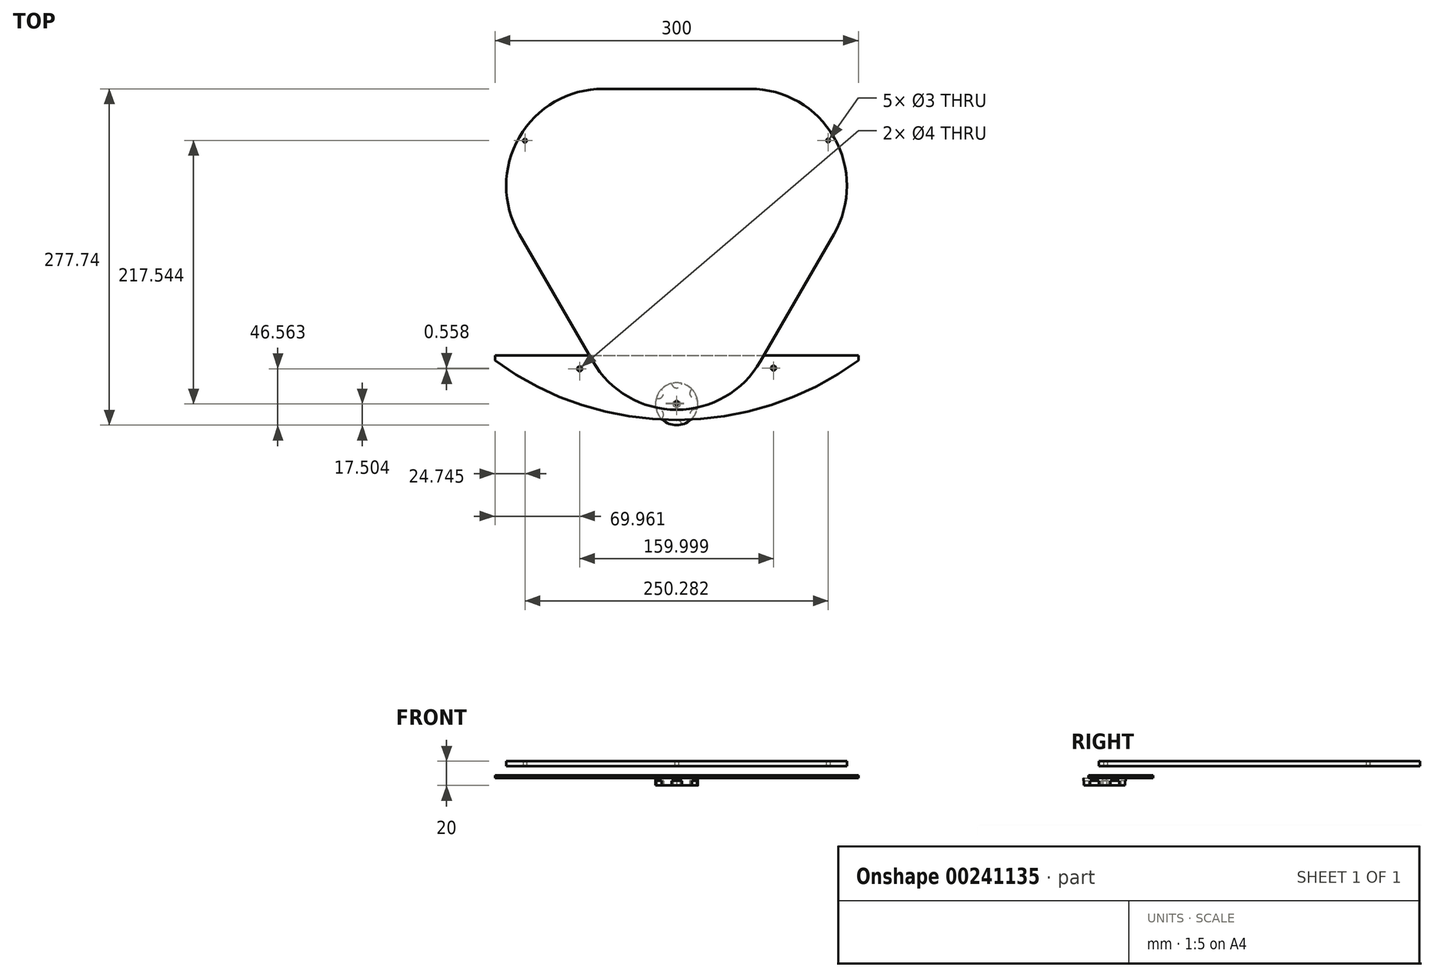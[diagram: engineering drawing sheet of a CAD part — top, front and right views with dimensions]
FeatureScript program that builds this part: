
annotation { "Feature Type Name" : "Feature", "Feature Type Description" : "" }
export const myFeature = defineFeature(function(context is Context, id is Id, definition is map)
    precondition{}
    {
        {
            var Q0;
            Q0=qCreatedBy(makeId("Top.planeOp"),FACE);
            var sketch = newSketch(context, id + "F0", { "sketchPlane" : qUnion([Q0])});
            skLineSegment(sketch, "E0.bottom", {"start": v(-210.81, -28.63) * mm, "end": v(89.19, -28.63) * mm});
            skCircle(sketch, "E1", {"center": v(-140.85, -39.57) * mm, "radius": 2 * mm});
            skCircle(sketch, "E2.MirrorC", {"center": v(19.15, -39) * mm, "radius": 2 * mm});
            skArc(sketch, "E3.2.3", {"start": v(-210.81, -32.82) * mm, "mid": v(-60.8, -81.83) * mm, "end": v(89.19, -32.72) * mm});
            skLineSegment(sketch, "E4", {"start": v(-210.81, -32.82) * mm, "end": v(-210.81, -28.63) * mm});
            skLineSegment(sketch, "E5", {"start": v(89.19, -32.72) * mm, "end": v(89.19, -28.63) * mm});
            skLineSegment(sketch, "E6.0", {"start": v(-210.81, -48.63) * mm, "end": v(89.19, -48.63) * mm, "construction": true});
            skCircle(sketch, "E7", {"center": v(-60.81, -68.63) * mm, "radius": 17.5 * mm});
            skPoint(sketch, "E7.centerSnap0", {"position": v(-60.81, -48.63) * mm});
            skCircle(sketch, "E8", {"center": v(-60.81, -68.63) * mm, "radius": 1.5 * mm});
            skSolve(sketch);
        }
        {
            var Q0;
            Q0=makeQuery(id+"F0.imprint","IMPRINT",FACE,{"disambiguationData":[TD([[makeQuery(id+"F0.imprint","IMPRINT",EDGE,{"derivedFrom":sQuery(id+"F0.wireOp",EDGE,"E0.bottom")}),-1.0]])]});
            var Q1;
            Q1=makeQuery(id+"F0.imprint","IMPRINT",FACE,{"disambiguationData":[TD([[makeQuery(id+"F0.imprint","IMPRINT",EDGE,{"derivedFrom":sQuery(id+"F0.wireOp",EDGE,"E8")}),-1.0]])]});
            extrude(context, id + "F1", {"entities" : qUnion([Q0, Q1]), "depth" : 2.5 * mm, "offsetDistance" : 25 * mm});
        }
        {
            var Q0;
            Q0=makeQuery(id+"F0.imprint","IMPRINT",FACE,{"disambiguationData":[TD([[makeQuery(id+"F0.imprint","IMPRINT",EDGE,{"derivedFrom":sQuery(id+"F0.wireOp",EDGE,"E8")}),-1.0]])]});
            var Q1;
            {var subQ0=sQuery(id+"F0.wireOp",EDGE,"E7");var subQ1=sQuery(id+"F0.wireOp",EDGE,"E3.2.3");var subQ2=makeQuery(id+"F0.imprint","INTERSECT",VERTEX,{"disambiguationData":[OD(0.0)],"derivedFrom":[subQ1,subQ0]});Q1=makeQuery(id+"F0.imprint","IMPRINT",FACE,{"disambiguationData":[TD([[makeQuery(id+"F0.imprint","IMPRINT",EDGE,{"disambiguationData":[TD([[subQ2,-1.0]])],"derivedFrom":subQ1}),-1.0]])]});}
            extrude(context, id + "F2", {"entities" : qUnion([Q0, Q1]), "oppositeDirection" : true, "depth" : 6 * mm, "offsetDistance" : 25 * mm});
        }
        {
            var Q0;
            Q0=qCreatedBy(makeId("Top.planeOp"),FACE);
            var sketch = newSketch(context, id + "F3", { "sketchPlane" : qUnion([Q0])});
            skArc(sketch, "E9", {"start": v(-173.75, 54.53) * mm, "mid": v(-160.45, 19.06) * mm, "end": v(-136.35, -10.17) * mm});
            skArc(sketch, "E10.2.1", {"start": v(-60.82, -62.9) * mm, "mid": v(-64.35, -71.43) * mm, "end": v(-55.82, -67.9) * mm});
            skArc(sketch, "E11.trimOffspring", {"start": v(-23.57, 185.39) * mm, "mid": v(-60.95, 191.6) * mm, "end": v(-98.3, 185.35) * mm});
            skArc(sketch, "E12.trimOffspring", {"start": v(14.66, -10.1) * mm, "mid": v(38.73, 19.16) * mm, "end": v(52, 54.64) * mm});
            skLineSegment(sketch, "E13", {"start": v(-136.35, -10.17) * mm, "end": v(-65.82, -67.9) * mm, "construction": true});
            skLineSegment(sketch, "E14", {"start": v(-55.82, -67.9) * mm, "end": v(14.66, -10.1) * mm});
            skLineSegment(sketch, "E15.1.0", {"start": v(52, 54.64) * mm, "end": v(66.72, 144.59) * mm, "construction": true});
            skArc(sketch, "E15.1.1", {"start": v(59.89, 146.42) * mm, "mid": v(69.05, 147.62) * mm, "end": v(61.72, 153.25) * mm});
            skLineSegment(sketch, "E15.1.2", {"start": v(61.72, 153.25) * mm, "end": v(-23.57, 185.39) * mm, "construction": true});
            skLineSegment(sketch, "E15.2.0", {"start": v(-98.3, 185.35) * mm, "end": v(-183.56, 153.13) * mm});
            skArc(sketch, "E15.2.1", {"start": v(-181.73, 146.3) * mm, "mid": v(-187.36, 153.63) * mm, "end": v(-188.56, 144.47) * mm});
            skLineSegment(sketch, "E15.2.2", {"start": v(-188.56, 144.47) * mm, "end": v(-173.75, 54.53) * mm, "construction": true});
            skCircle(sketch, "E16", {"center": v(-186.06, 148.8) * mm, "radius": 1.5 * mm});
            skCircle(sketch, "E17", {"center": v(-60.82, -67.9) * mm, "radius": 1.5 * mm});
            skCircle(sketch, "E18", {"center": v(64.22, 148.92) * mm, "radius": 1.5 * mm});
            skCircle(sketch, "E19.cCircle", {"center": v(-60.89, 76.6) * mm, "radius": 115 * mm, "construction": true});
            skLineSegment(sketch, "E19.0", {"start": v(-121.51, 191.6) * mm, "end": v(-0.27, 191.6) * mm});
            skLineSegment(sketch, "E19.1", {"start": v(69.02, 71.6) * mm, "end": v(8.4, -33.4) * mm});
            skLineSegment(sketch, "E19.2", {"start": v(-130.17, -33.4) * mm, "end": v(-190.8, 71.6) * mm});
            skPoint(sketch, "E19.0.midPoint", {"position": v(-60.89, 191.6) * mm});
            skPoint(sketch, "E20.visualSharp", {"position": v(-260.07, 191.6) * mm});
            skArc(sketch, "E20.filletArc", {"start": v(-121.51, 191.6) * mm, "mid": v(-190.8, 151.6) * mm, "end": v(-190.8, 71.6) * mm});
            skPoint(sketch, "E21.visualSharp", {"position": v(138.3, 191.6) * mm});
            skArc(sketch, "E21.filletArc", {"start": v(69.02, 71.6) * mm, "mid": v(69.02, 151.6) * mm, "end": v(-0.27, 191.6) * mm});
            skPoint(sketch, "E22.visualSharp", {"position": v(-60.89, -153.4) * mm});
            skArc(sketch, "E22.filletArc", {"start": v(-130.17, -33.4) * mm, "mid": v(-60.89, -73.4) * mm, "end": v(8.4, -33.4) * mm});
            skSolve(sketch);
        }
        {
            var Q0;
            Q0=makeQuery(id+"F3.imprint","IMPRINT",FACE,{"disambiguationData":[TD([[makeQuery(id+"F3.imprint","IMPRINT",EDGE,{"derivedFrom":sQuery(id+"F3.wireOp",EDGE,"E16")}),-1.0]])]});
            extrude(context, id + "F4", {"entities" : qUnion([Q0]), "depth" : 4 * mm, "offsetDistance" : 25 * mm});
        }
        {
            var Q0;
            Q0=makeQuery(id+"F4.opExtrude","SWEPT_BODY",BODY,{"disambiguationData":[OSD([sQuery(id+"F3.wireOp",EDGE,"E9"),sQuery(id+"F3.wireOp",EDGE,"E10.2.1"),sQuery(id+"F3.wireOp",EDGE,"E11.trimOffspring"),sQuery(id+"F3.wireOp",EDGE,"E12.trimOffspring"),sQuery(id+"F3.wireOp",EDGE,"E13"),sQuery(id+"F3.wireOp",EDGE,"E14"),sQuery(id+"F3.wireOp",EDGE,"E15.1.0"),sQuery(id+"F3.wireOp",EDGE,"E15.1.1"),sQuery(id+"F3.wireOp",EDGE,"E15.1.2"),sQuery(id+"F3.wireOp",EDGE,"E15.2.0"),sQuery(id+"F3.wireOp",EDGE,"E15.2.1"),sQuery(id+"F3.wireOp",EDGE,"E15.2.2"),sQuery(id+"F3.wireOp",EDGE,"E16"),sQuery(id+"F3.wireOp",EDGE,"E17"),sQuery(id+"F3.wireOp",EDGE,"E18")])]});
            transform(context, id + "F5", {"entities" : qUnion([Q0]), "transformType" : TransformType.TRANSLATION_3D, "dx" : 0 * mm, "dy" : 0 * mm, "dz" : 10 * mm, "makeCopy" : false});
        }
        {
            var Q0;
            Q0=makeQuery(id+"F2.opExtrude","CAP_FACE",FACE,{"disambiguationData":[OSD([sQuery(id+"F0.wireOp",EDGE,"E7"),sQuery(id+"F0.wireOp",EDGE,"E8")])],"isStart":false});
            var sketch = newSketch(context, id + "F6", { "sketchPlane" : qUnion([Q0])});
            skCircle(sketch, "E23.cCircle", {"center": v(-60.81, 68.63) * mm, "radius": 2.75 * mm, "construction": true});
            skLineSegment(sketch, "E23.0", {"start": v(-63.56, 67.04) * mm, "end": v(-63.56, 70.21) * mm});
            skLineSegment(sketch, "E23.1", {"start": v(-63.56, 70.21) * mm, "end": v(-60.81, 71.8) * mm});
            skLineSegment(sketch, "E23.2", {"start": v(-60.81, 71.8) * mm, "end": v(-58.06, 70.21) * mm});
            skLineSegment(sketch, "E23.3", {"start": v(-58.06, 70.21) * mm, "end": v(-58.06, 67.04) * mm});
            skLineSegment(sketch, "E23.4", {"start": v(-58.06, 67.04) * mm, "end": v(-60.81, 65.45) * mm});
            skLineSegment(sketch, "E23.5", {"start": v(-60.81, 65.45) * mm, "end": v(-63.56, 67.04) * mm});
            skPoint(sketch, "E23.0.midPoint", {"position": v(-63.56, 68.63) * mm});
            skCircle(sketch, "E24", {"center": v(-60.81, 86.13) * mm, "radius": 4.3 * mm});
            skCircle(sketch, "E25.1.0", {"center": v(-75.97, 77.38) * mm, "radius": 4.3 * mm});
            skCircle(sketch, "E25.2.0", {"center": v(-75.97, 59.88) * mm, "radius": 4.3 * mm});
            skCircle(sketch, "E25.3.0", {"center": v(-60.81, 51.13) * mm, "radius": 4.3 * mm});
            skCircle(sketch, "E25.4.0", {"center": v(-45.66, 59.88) * mm, "radius": 4.3 * mm});
            skCircle(sketch, "E25.5.0", {"center": v(-45.66, 77.38) * mm, "radius": 4.3 * mm});
            skSolve(sketch);
        }
        {
            var Q0;
            Q0=makeQuery(id+"F6.imprint","IMPRINT",FACE,{"disambiguationData":[TD([[makeQuery(id+"F6.imprint","IMPRINT",EDGE,{"derivedFrom":sQuery(id+"F6.wireOp",EDGE,"E23.0")}),-1.0]])]});
            var Q1;
            {var subQ0=sQuery(id+"F6.wireOp",EDGE,"E25.2.0");var subQ1=makeQuery(id+"F2.opExtrude","CAP_EDGE",EDGE,{"disambiguationData":[OSD([sQuery(id+"F0.wireOp",EDGE,"E7")])],"isStart":false});var subQ2=makeQuery(id+"F6.imprint","INTERSECT",VERTEX,{"disambiguationData":[OD(0.0)],"derivedFrom":[subQ1,subQ0]});Q1=makeQuery(id+"F6.imprint","IMPRINT",FACE,{"disambiguationData":[TD([[makeQuery(id+"F6.imprint","IMPRINT",EDGE,{"disambiguationData":[TD([[subQ2,1.0]])],"derivedFrom":subQ0}),1.0]])]});}
            var Q2;
            {var subQ0=sQuery(id+"F6.wireOp",EDGE,"E25.1.0");var subQ1=makeQuery(id+"F2.opExtrude","CAP_EDGE",EDGE,{"disambiguationData":[OSD([sQuery(id+"F0.wireOp",EDGE,"E7")])],"isStart":false});var subQ2=makeQuery(id+"F6.imprint","INTERSECT",VERTEX,{"disambiguationData":[OD(0.0)],"derivedFrom":[subQ1,subQ0]});Q2=makeQuery(id+"F6.imprint","IMPRINT",FACE,{"disambiguationData":[TD([[makeQuery(id+"F6.imprint","IMPRINT",EDGE,{"disambiguationData":[TD([[subQ2,-1.0]])],"derivedFrom":subQ0}),1.0]])]});}
            var Q3;
            {var subQ0=sQuery(id+"F6.wireOp",EDGE,"E24");var subQ1=makeQuery(id+"F2.opExtrude","CAP_EDGE",EDGE,{"disambiguationData":[OSD([sQuery(id+"F0.wireOp",EDGE,"E7")])],"isStart":false});var subQ2=makeQuery(id+"F6.imprint","INTERSECT",VERTEX,{"disambiguationData":[OD(0.0)],"derivedFrom":[subQ1,subQ0]});Q3=makeQuery(id+"F6.imprint","IMPRINT",FACE,{"disambiguationData":[TD([[makeQuery(id+"F6.imprint","IMPRINT",EDGE,{"disambiguationData":[TD([[subQ2,-1.0]])],"derivedFrom":subQ0}),1.0]])]});}
            var Q4;
            {var subQ0=sQuery(id+"F6.wireOp",EDGE,"E25.5.0");var subQ1=makeQuery(id+"F2.opExtrude","CAP_EDGE",EDGE,{"disambiguationData":[OSD([sQuery(id+"F0.wireOp",EDGE,"E7")])],"isStart":false});var subQ2=makeQuery(id+"F6.imprint","INTERSECT",VERTEX,{"disambiguationData":[OD(0.0)],"derivedFrom":[subQ1,subQ0]});Q4=makeQuery(id+"F6.imprint","IMPRINT",FACE,{"disambiguationData":[TD([[makeQuery(id+"F6.imprint","IMPRINT",EDGE,{"disambiguationData":[TD([[subQ2,-1.0]])],"derivedFrom":subQ0}),1.0]])]});}
            var Q5;
            {var subQ0=sQuery(id+"F6.wireOp",EDGE,"E25.4.0");var subQ1=makeQuery(id+"F2.opExtrude","CAP_EDGE",EDGE,{"disambiguationData":[OSD([sQuery(id+"F0.wireOp",EDGE,"E7")])],"isStart":false});var subQ2=makeQuery(id+"F6.imprint","INTERSECT",VERTEX,{"disambiguationData":[OD(0.0)],"derivedFrom":[subQ1,subQ0]});Q5=makeQuery(id+"F6.imprint","IMPRINT",FACE,{"disambiguationData":[TD([[makeQuery(id+"F6.imprint","IMPRINT",EDGE,{"disambiguationData":[TD([[subQ2,1.0]])],"derivedFrom":subQ0}),1.0]])]});}
            var Q6;
            {var subQ0=sQuery(id+"F6.wireOp",EDGE,"E25.3.0");var subQ1=makeQuery(id+"F2.opExtrude","CAP_EDGE",EDGE,{"disambiguationData":[OSD([sQuery(id+"F0.wireOp",EDGE,"E7")])],"isStart":false});var subQ2=makeQuery(id+"F6.imprint","INTERSECT",VERTEX,{"disambiguationData":[OD(0.0)],"derivedFrom":[subQ1,subQ0]});Q6=makeQuery(id+"F6.imprint","IMPRINT",FACE,{"disambiguationData":[TD([[makeQuery(id+"F6.imprint","IMPRINT",EDGE,{"disambiguationData":[TD([[subQ2,1.0]])],"derivedFrom":subQ0}),1.0]])]});}
            extrude(context, id + "F7", {"entities" : qUnion([Q0, Q1, Q2, Q3, Q4, Q5, Q6]), "operationType" : NewBodyOperationType.REMOVE, "oppositeDirection" : true, "depth" : 4 * mm, "offsetDistance" : 25 * mm});
        }
    });
